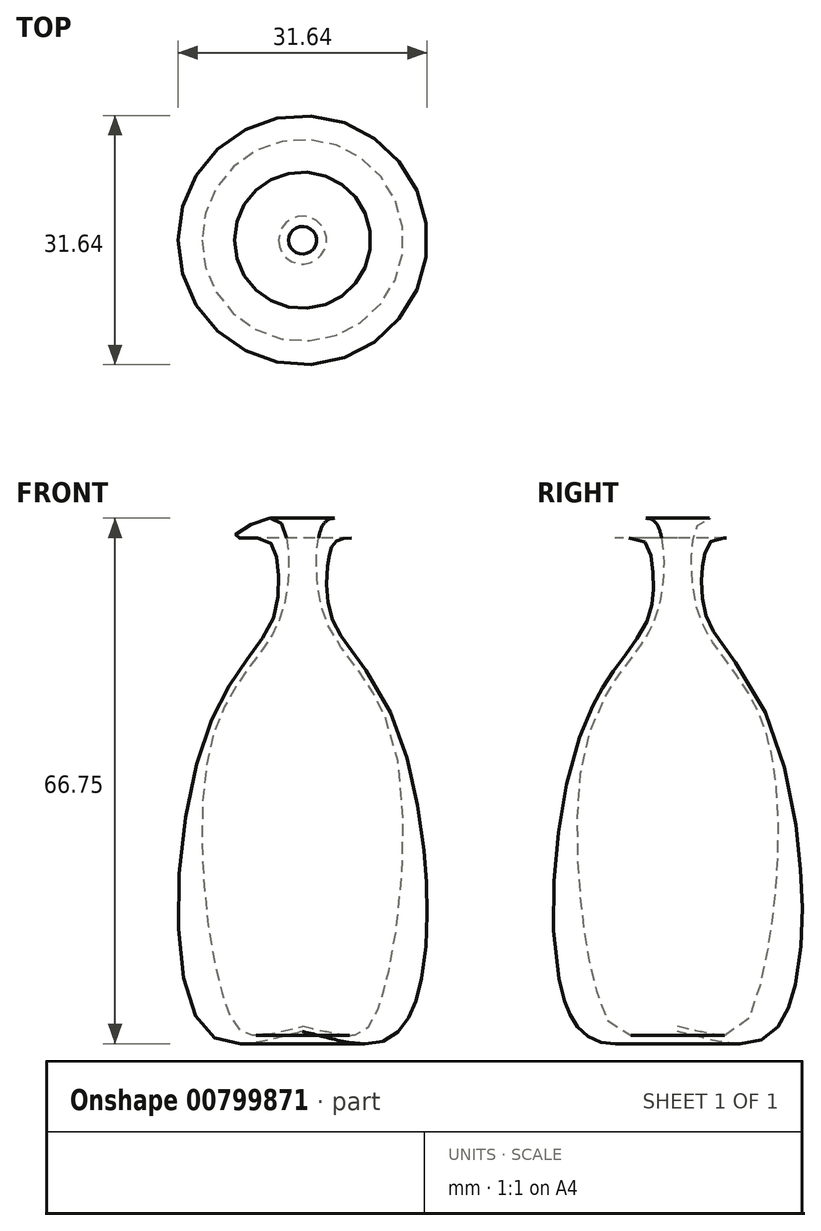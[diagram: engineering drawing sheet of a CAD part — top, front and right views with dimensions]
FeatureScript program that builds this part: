
annotation { "Feature Type Name" : "Feature", "Feature Type Description" : "" }
export const myFeature = defineFeature(function(context is Context, id is Id, definition is map)
    precondition{}
    {
        {
            var Q0;
            Q0=qCreatedBy(makeId("Front.planeOp"),FACE);
            var sketch = newSketch(context, id + "F0", { "sketchPlane" : qUnion([Q0])});
            skFitSpline(sketch, "E0", {"points": [v(0, 0) * mm, v(-12.2, 0) * mm, v(-12.1, 38.33) * mm, v(-3.79, 52.34) * mm, v(-3.25, 59.61) * mm, v(-4.84, 62.58) * mm, v(-8.67, 62.83) * mm, v(-4.37, 65.19) * mm, v(-2.28, 63.66) * mm, v(-1.92, 56.73) * mm, v(-4.2, 49.83) * mm, v(-11.78, 36.05) * mm, v(-9.12, 1.8) * mm, v(0, 0.64) * mm], "startDerivative": vector(-140.6, -30.23) * mm, "endDerivative": vector(257.17, 61.46) * mm});
            skLineSegment(sketch, "E1", {"start": v(0, 0) * mm, "end": v(0, 83.12) * mm, "construction": true});
            skLineSegment(sketch, "E2", {"start": v(0, 0) * mm, "end": v(0, 0.64) * mm});
            skSolve(sketch);
        }
        {
            var Q0;
            Q0 = qSketchRegion(id + "F0", true);
            var Q1;
            Q1=sQuery(id+"F0.wireOp",EDGE,"E1");
            revolve(context, id + "F1", {"surfaceOperationType" : NewSurfaceOperationType.NEW, "entities" : qUnion([Q0]), "axis" : qUnion([Q1]), "revolveType" : RevolveType.FULL});
        }
    });
